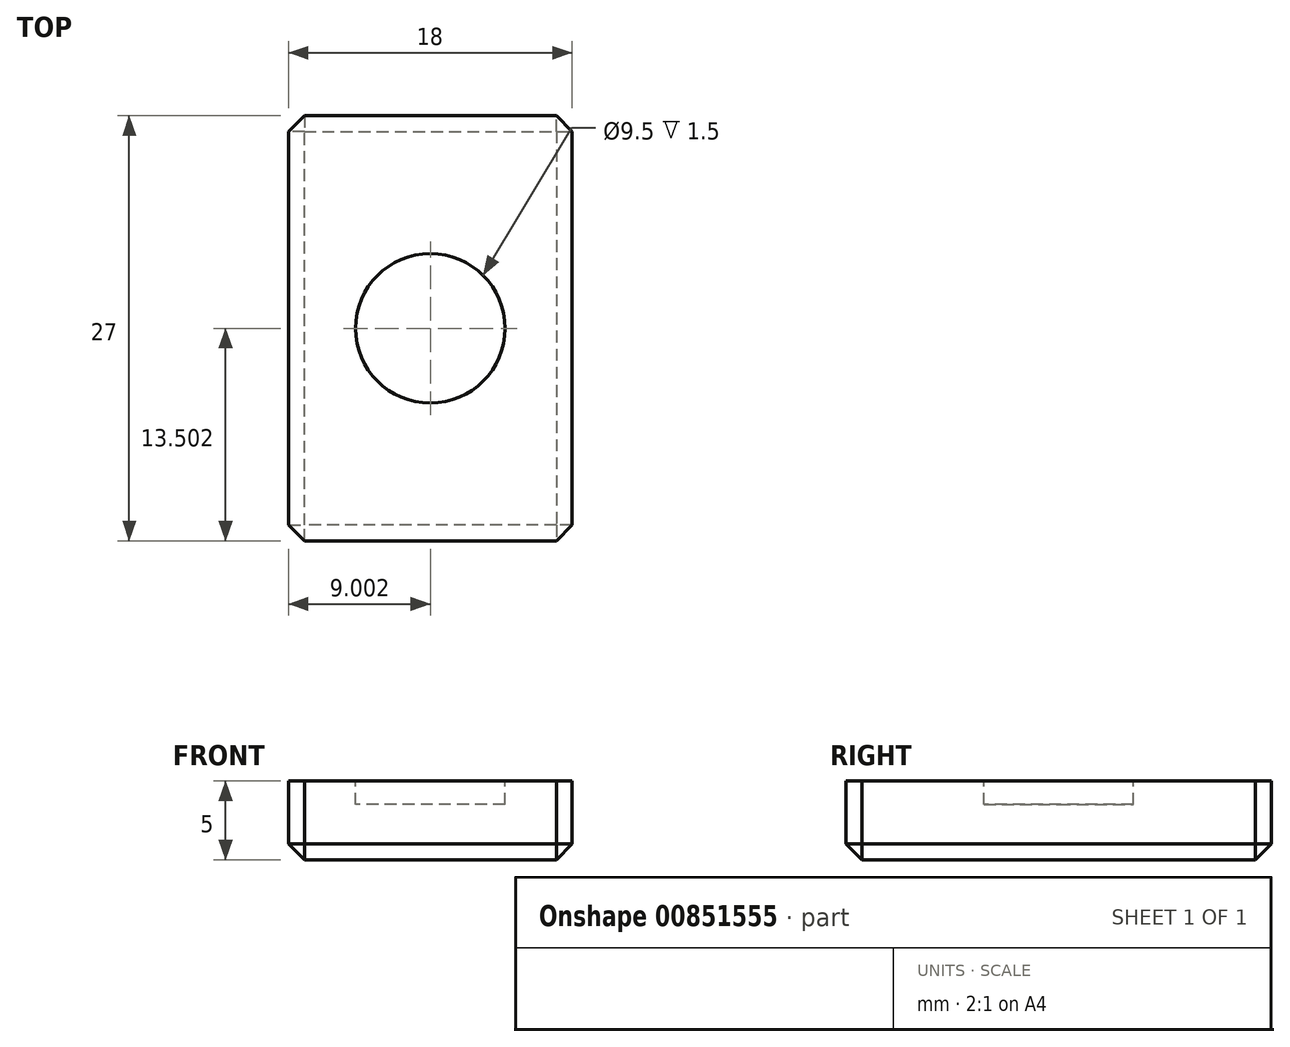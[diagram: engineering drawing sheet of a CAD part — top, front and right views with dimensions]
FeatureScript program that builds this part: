
annotation { "Feature Type Name" : "Feature", "Feature Type Description" : "" }
export const myFeature = defineFeature(function(context is Context, id is Id, definition is map)
    precondition{}
    {
        {
            var Q0;
            Q0=qCreatedBy(makeId("Top.planeOp"),FACE);
            var sketch = newSketch(context, id + "F0", { "sketchPlane" : qUnion([Q0])});
            skLineSegment(sketch, "E0.bottom", {"start": v(4.32, 3.92) * mm, "end": v(22.32, 3.92) * mm});
            skLineSegment(sketch, "E0.top", {"start": v(4.32, 30.92) * mm, "end": v(22.32, 30.92) * mm});
            skLineSegment(sketch, "E0.left", {"start": v(4.32, 3.92) * mm, "end": v(4.32, 30.92) * mm});
            skLineSegment(sketch, "E0.right", {"start": v(22.32, 3.92) * mm, "end": v(22.32, 30.92) * mm});
            skSolve(sketch);
        }
        {
            var Q0;
            Q0=makeQuery(id+"F0.imprint","IMPRINT",FACE,{"disambiguationData":[TD([[makeQuery(id+"F0.imprint","IMPRINT",EDGE,{"derivedFrom":sQuery(id+"F0.wireOp",EDGE,"E0.bottom")}),1.0]])]});
            extrude(context, id + "F1", {"entities" : qUnion([Q0]), "depth" : 5 * mm, "offsetDistance" : 25 * mm});
        }
        {
            var Q0;
            Q0=makeQuery(id+"F1.opExtrude","SWEPT_EDGE",EDGE,{"disambiguationData":[OSD([sQuery(id+"F0.wireOp",EDGE,"E0.top"),sQuery(id+"F0.wireOp",EDGE,"E0.left")])]});
            var Q1;
            Q1=makeQuery(id+"F1.opExtrude","SWEPT_EDGE",EDGE,{"disambiguationData":[OSD([sQuery(id+"F0.wireOp",EDGE,"E0.bottom"),sQuery(id+"F0.wireOp",EDGE,"E0.left")])]});
            var Q2;
            Q2=makeQuery(id+"F1.opExtrude","SWEPT_EDGE",EDGE,{"disambiguationData":[OSD([sQuery(id+"F0.wireOp",EDGE,"E0.bottom"),sQuery(id+"F0.wireOp",EDGE,"E0.right")])]});
            var Q3;
            Q3=makeQuery(id+"F1.opExtrude","SWEPT_EDGE",EDGE,{"disambiguationData":[OSD([sQuery(id+"F0.wireOp",EDGE,"E0.top"),sQuery(id+"F0.wireOp",EDGE,"E0.right")])]});
            var Q4;
            Q4=makeQuery(id+"F1.opExtrude","CAP_EDGE",EDGE,{"disambiguationData":[OSD([sQuery(id+"F0.wireOp",EDGE,"E0.right")])],"isStart":true});
            var Q5;
            Q5=makeQuery(id+"F1.opExtrude","CAP_EDGE",EDGE,{"disambiguationData":[OSD([sQuery(id+"F0.wireOp",EDGE,"E0.left")])],"isStart":true});
            var Q6;
            Q6=makeQuery(id+"F1.opExtrude","CAP_FACE",FACE,{"disambiguationData":[OSD([sQuery(id+"F0.wireOp",EDGE,"E0.bottom"),sQuery(id+"F0.wireOp",EDGE,"E0.top"),sQuery(id+"F0.wireOp",EDGE,"E0.left"),sQuery(id+"F0.wireOp",EDGE,"E0.right")])],"isStart":true});
            chamfer(context, id + "F2", {"entities" : qUnion([Q0, Q1, Q2, Q3, Q4, Q5, Q6]), "width" : 1 * mm, "tangentPropagation" : true});
        }
        {
            var Q0;
            Q0=makeQuery(id+"F1.opExtrude","CAP_FACE",FACE,{"disambiguationData":[OSD([sQuery(id+"F0.wireOp",EDGE,"E0.bottom"),sQuery(id+"F0.wireOp",EDGE,"E0.top"),sQuery(id+"F0.wireOp",EDGE,"E0.left"),sQuery(id+"F0.wireOp",EDGE,"E0.right")])],"isStart":false});
            var sketch = newSketch(context, id + "F3", { "sketchPlane" : qUnion([Q0])});
            skCircle(sketch, "E1", {"center": v(13.32, 17.42) * mm, "radius": 4.75 * mm});
            skSolve(sketch);
        }
        {
            var Q0;
            Q0=makeQuery(id+"F3.imprint","IMPRINT",FACE,{"disambiguationData":[TD([[makeQuery(id+"F3.imprint","IMPRINT",EDGE,{"derivedFrom":sQuery(id+"F3.wireOp",EDGE,"E1")}),1.0]])]});
            extrude(context, id + "F4", {"entities" : qUnion([Q0]), "operationType" : NewBodyOperationType.REMOVE, "oppositeDirection" : true, "depth" : 1.5 * mm, "offsetDistance" : 25 * mm});
        }
    });
